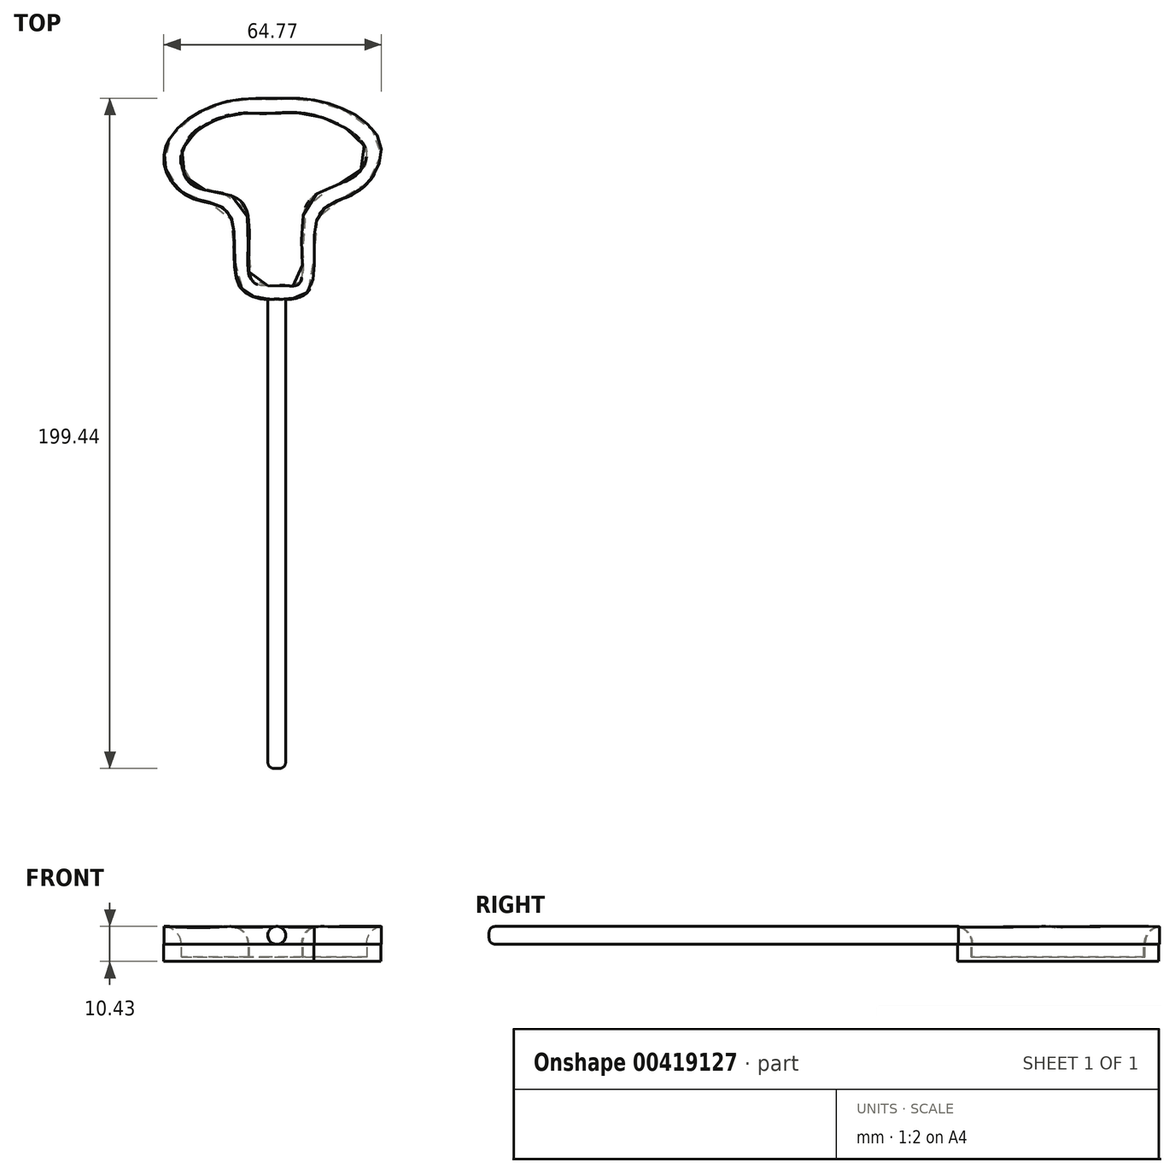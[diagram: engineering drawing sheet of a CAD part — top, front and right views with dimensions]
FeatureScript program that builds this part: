
annotation { "Feature Type Name" : "Feature", "Feature Type Description" : "" }
export const myFeature = defineFeature(function(context is Context, id is Id, definition is map)
    precondition{}
    {
        {
            var Q0;
            Q0=qCreatedBy(makeId("Front.planeOp"),FACE);
            var sketch = newSketch(context, id + "F0", { "sketchPlane" : qUnion([Q0])});
            skCircle(sketch, "E0", {"center": v(-24.45, 2.68) * mm, "radius": 2.67 * mm});
            skSolve(sketch);
        }
        {
            var Q0;
            Q0 = qSketchRegion(id + "F0", true);
            extrude(context, id + "F1", {"entities" : qUnion([Q0]), "depth" : 139.7 * mm, "offsetDistance" : 25.4 * mm});
        }
        {
            var Q0;
            Q0=makeQuery(id+"F1.opExtrude","CAP_EDGE",EDGE,{"disambiguationData":[OSD([sQuery(id+"F0.wireOp",EDGE,"E0")])],"isStart":false});
            fillet(context, id + "F2", {"entities" : qUnion([Q0]), "radius" : 2.18 * mm, "tangentPropagation" : true, "rho" : 0.5, "crossSection" : FilletCrossSection.CONIC, "allowEdgeOverflow" : false});
        }
        {
            var Q0;
            Q0=qCreatedBy(makeId("Top.planeOp"),FACE);
            var sketch = newSketch(context, id + "F3", { "sketchPlane" : qUnion([Q0])});
            skFitSpline(sketch, "E1", {"points": [v(-27.08, 0) * mm, v(-35.68, 4.44) * mm, v(-38.48, 25.38) * mm, v(-50.69, 30.65) * mm, v(-57.94, 42.2) * mm, v(-51.02, 53.42) * mm, v(-38.15, 59.02) * mm, v(-29.57, 59.68) * mm, v(-22.98, 59.68) * mm, v(-14.07, 59.35) * mm, v(0, 54.08) * mm, v(6.69, 44.54) * mm, v(0, 32.3) * mm, v(-12.09, 24.72) * mm, v(-14.4, 3.27) * mm, v(-21.66, 0) * mm, v(-27.08, 0) * mm]});
            skFitSpline(sketch, "E2", {"points": [v(-27.02, 4.02) * mm, v(-32.38, 6.2) * mm, v(-34.56, 28.24) * mm, v(-48.65, 33.4) * mm, v(-53.02, 41.93) * mm, v(-48.85, 49.87) * mm, v(-37.34, 55.04) * mm, v(-29.6, 55.23) * mm, v(-23.24, 55.43) * mm, v(-14.9, 55.04) * mm, v(-3, 50.27) * mm, v(2.17, 43.72) * mm, v(-2, 35.98) * mm, v(-15.7, 27.84) * mm, v(-17.49, 5) * mm, v(-21.85, 4.02) * mm, v(-27.02, 4.02) * mm]});
            skSolve(sketch);
        }
        {
            var Q0;
            Q0 = qSketchRegion(id + "F3", true);
            extrude(context, id + "F4", {"entities" : qUnion([Q0]), "operationType" : NewBodyOperationType.ADD, "depth" : 5.33 * mm, "offsetDistance" : 25.4 * mm});
        }
        {
            var Q0;
            Q0=makeQuery(id+"F4.opExtrude","CAP_EDGE",EDGE,{"disambiguationData":[OSD([sQuery(id+"F3.wireOp",EDGE,"E2")])],"isStart":false});
            fillet(context, id + "F5", {"entities" : qUnion([Q0]), "radius" : 5.08 * mm, "tangentPropagation" : true, "allowEdgeOverflow" : false});
        }
        {
            var Q0;
            Q0=qCreatedBy(makeId("Top.planeOp"),FACE);
            cPlane(context, id + "F6", {"entities" : qUnion([Q0]), "cplaneType" : CPlaneType.OFFSET, "offset" : 0 * mm, "width" : 152.4 * mm, "height" : 152.4 * mm});
        }
        {
            var Q0;
            Q0=qCreatedBy(id+"F6.planeOp",FACE);
            var sketch = newSketch(context, id + "F7", { "sketchPlane" : qUnion([Q0])});
            skFitSpline(sketch, "E3", {"points": [v(-27.21, -0.22) * mm, v(-35.8, 4.22) * mm, v(-38.6, 25.16) * mm, v(-50.81, 30.44) * mm, v(-58.07, 41.98) * mm, v(-51.14, 53.2) * mm, v(-38.28, 58.8) * mm, v(-29.7, 59.47) * mm, v(-23.1, 59.47) * mm, v(-14.2, 59.14) * mm, v(-0.13, 53.86) * mm, v(6.56, 44.32) * mm, v(-0.13, 32.09) * mm, v(-12.22, 24.5) * mm, v(-14.53, 3.06) * mm, v(-21.79, -0.22) * mm, v(-27.21, -0.22) * mm]});
            skSolve(sketch);
        }
        {
            var Q0;
            Q0 = qSketchRegion(id + "F7", true);
            extrude(context, id + "F8", {"entities" : qUnion([Q0]), "operationType" : NewBodyOperationType.ADD, "oppositeDirection" : true, "depth" : 5.08 * mm, "offsetDistance" : 25.4 * mm});
        }
        {
            var Q0;
            Q0=qCreatedBy(id+"F6.planeOp",FACE);
            var sketch = newSketch(context, id + "F9", { "sketchPlane" : qUnion([Q0])});
            skFitSpline(sketch, "E4", {"points": [v(-26.7, 3.91) * mm, v(-32.07, 6.1) * mm, v(-34.25, 28.13) * mm, v(-48.35, 33.3) * mm, v(-52.72, 41.83) * mm, v(-48.55, 49.77) * mm, v(-37.03, 54.93) * mm, v(-29.3, 55.13) * mm, v(-22.94, 55.33) * mm, v(-14.6, 54.93) * mm, v(-2.69, 50.17) * mm, v(2.47, 43.62) * mm, v(-1.7, 35.87) * mm, v(-15.4, 27.74) * mm, v(-17.18, 4.9) * mm, v(-21.55, 3.91) * mm, v(-26.7, 3.91) * mm]});
            skSolve(sketch);
        }
        {
            var Q0;
            Q0 = qSketchRegion(id + "F9", true);
            extrude(context, id + "F10", {"entities" : qUnion([Q0]), "operationType" : NewBodyOperationType.REMOVE, "oppositeDirection" : true, "depth" : 3.8 * mm, "offsetDistance" : 25.4 * mm});
        }
    });
